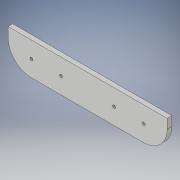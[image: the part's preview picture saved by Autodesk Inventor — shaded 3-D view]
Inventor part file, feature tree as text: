
AUTODESK INVENTOR PART (.ipt)
format: ipt  version: 2019 (Build 230136000, 136)  size: 117,760 bytes
history: native  units: in
note: dims shown in document units (in); Inventor stores cm internally (conversion verified against a paired STEP export)
features: sketch x2, extrude x1, hole x1
ambient origin geometry x8: Origin, YZ Plane, XZ Plane, XY Plane, X Axis, Y Axis, Z Axis, Center Point
bodies: Solid1 (feature_tree)
feature tree (4):
  extrude  "Extrusion1"  Depth=3.5in
  hole  "Hole1"  [1 undecoded]
  sketch  "Sketch1"  dims[d0=17.0in d1=3.5in]
  sketch  "Sketch2"  dims[d2=2.5in d3=2.5in d4=0.5in d5=0.0in d6=3.5in d7=1.75in d8=1.75in d9=1.75in d10=1.75in d11=17.0in d12=2.5in d13=5.6667in d14=5.6667in d15=2.5in d16=0.311in d17=0.75in d18=0.375in d19=0.25in d20=0.5635in d21=1.0in d22=0.8108in]
note: 1 required parameter value undecoded (feature->parameter linkage not recoverable at this tier; creation-order binding heuristic only, values carry confidence <= 0.55)
